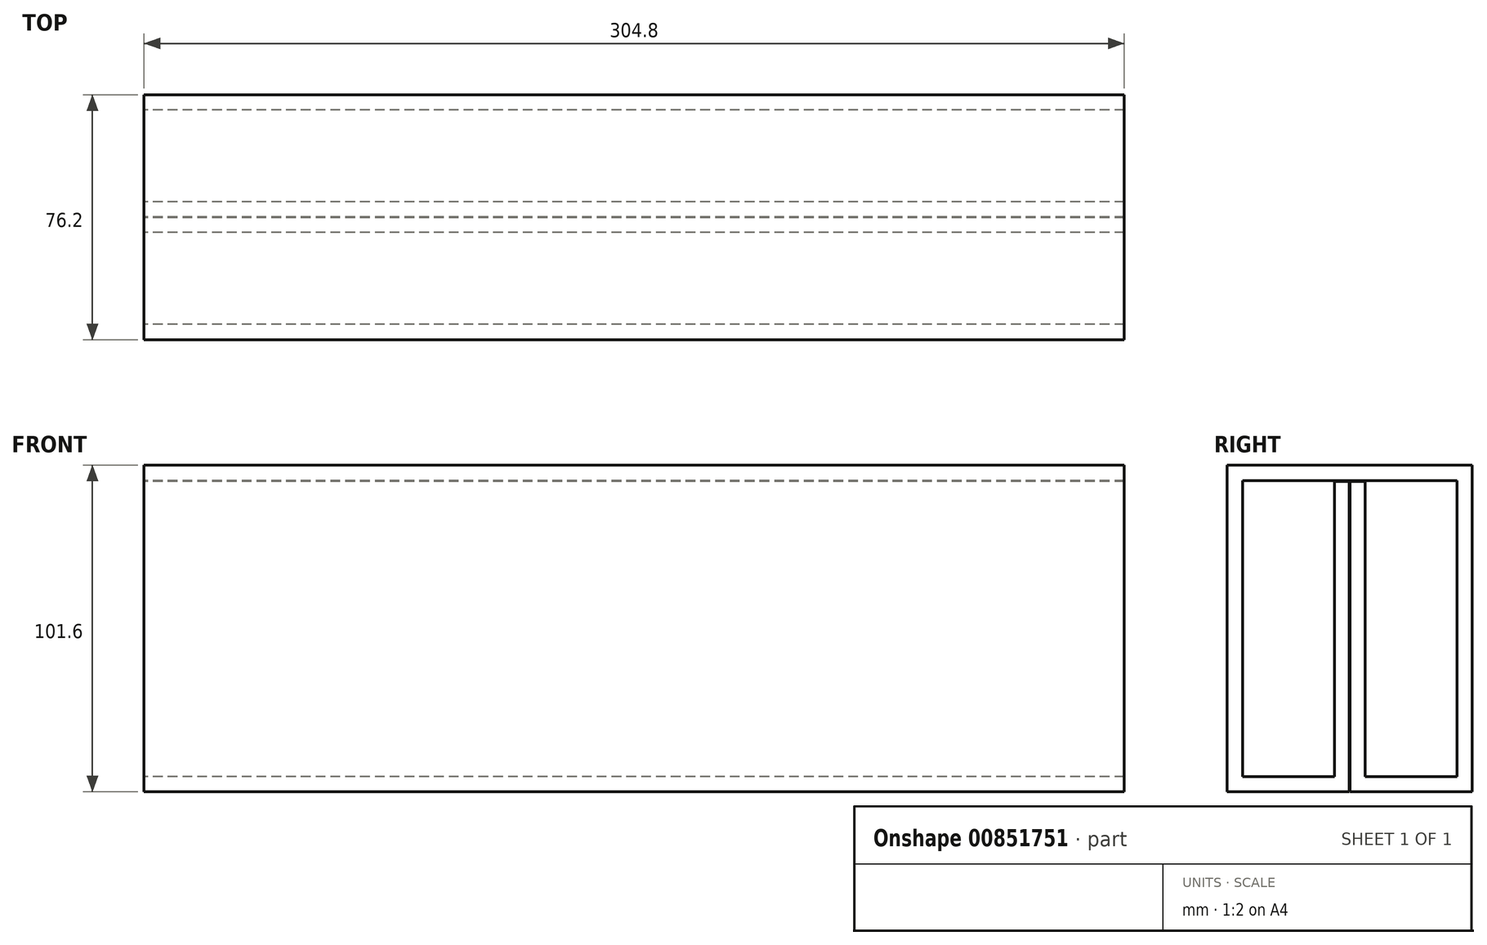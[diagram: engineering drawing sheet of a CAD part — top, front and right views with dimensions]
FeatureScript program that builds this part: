
annotation { "Feature Type Name" : "Feature", "Feature Type Description" : "" }
export const myFeature = defineFeature(function(context is Context, id is Id, definition is map)
    precondition{}
    {
        {
            var Q0;
            Q0=qCreatedBy(makeId("Right.planeOp"),FACE);
            var sketch = newSketch(context, id + "F0", { "sketchPlane" : qUnion([Q0])});
            skLineSegment(sketch, "E0", {"start": v(0, 0) * mm, "end": v(0, 126.35) * mm, "construction": true});
            skLineSegment(sketch, "E1.bottom", {"start": v(-38.1, 101.6) * mm, "end": v(38.1, 101.6) * mm});
            skLineSegment(sketch, "E1.top", {"start": v(-38.1, 0) * mm, "end": v(-0.13, 0) * mm});
            skLineSegment(sketch, "E1.left", {"start": v(-38.1, 101.6) * mm, "end": v(-38.1, 0) * mm});
            skLineSegment(sketch, "E2.0", {"start": v(-33.34, 96.84) * mm, "end": v(33.34, 96.84) * mm});
            skLineSegment(sketch, "E2.1", {"start": v(-33.34, 96.84) * mm, "end": v(-33.34, 4.76) * mm});
            skLineSegment(sketch, "E2.2", {"start": v(-33.34, 4.76) * mm, "end": v(-4.76, 4.76) * mm});
            skLineSegment(sketch, "E2.3", {"start": v(-4.76, 96.58) * mm, "end": v(-4.76, 4.76) * mm});
            skLineSegment(sketch, "E3.MirrorCS", {"start": v(38.1, 101.6) * mm, "end": v(38.1, 0) * mm});
            skLineSegment(sketch, "E4.MirrorCS", {"start": v(4.76, 96.58) * mm, "end": v(4.76, 4.76) * mm});
            skLineSegment(sketch, "E5.MirrorCS", {"start": v(33.34, 4.76) * mm, "end": v(4.76, 4.76) * mm});
            skLineSegment(sketch, "E6.MirrorCS", {"start": v(33.34, 96.84) * mm, "end": v(33.34, 4.76) * mm});
            skLineSegment(sketch, "E7.left", {"start": v(-0.13, 0) * mm, "end": v(-0.13, 96.58) * mm});
            skLineSegment(sketch, "E7.right", {"start": v(0.13, 0) * mm, "end": v(0.13, 96.58) * mm});
            skLineSegment(sketch, "E8.trimOffspring", {"start": v(0.13, 0) * mm, "end": v(38.1, 0) * mm});
            skLineSegment(sketch, "E9", {"start": v(-4.76, 96.58) * mm, "end": v(-0.13, 96.58) * mm});
            skPoint(sketch, "E10.orphan", {"position": v(4.76, 96.84) * mm});
            skLineSegment(sketch, "E11.trimOffspring", {"start": v(0.13, 96.58) * mm, "end": v(4.76, 96.58) * mm});
            skPoint(sketch, "E12.orphan", {"position": v(-4.76, 96.84) * mm});
            skSolve(sketch);
        }
        {
            var Q0;
            Q0=qSketchRegion(id+"F0",true);
            extrude(context, id + "F1", {"entities" : qUnion([Q0]), "endBound" : BoundingType.SYMMETRIC, "depth" : 304.8 * mm, "offsetDistance" : 25.4 * mm});
        }
    });
